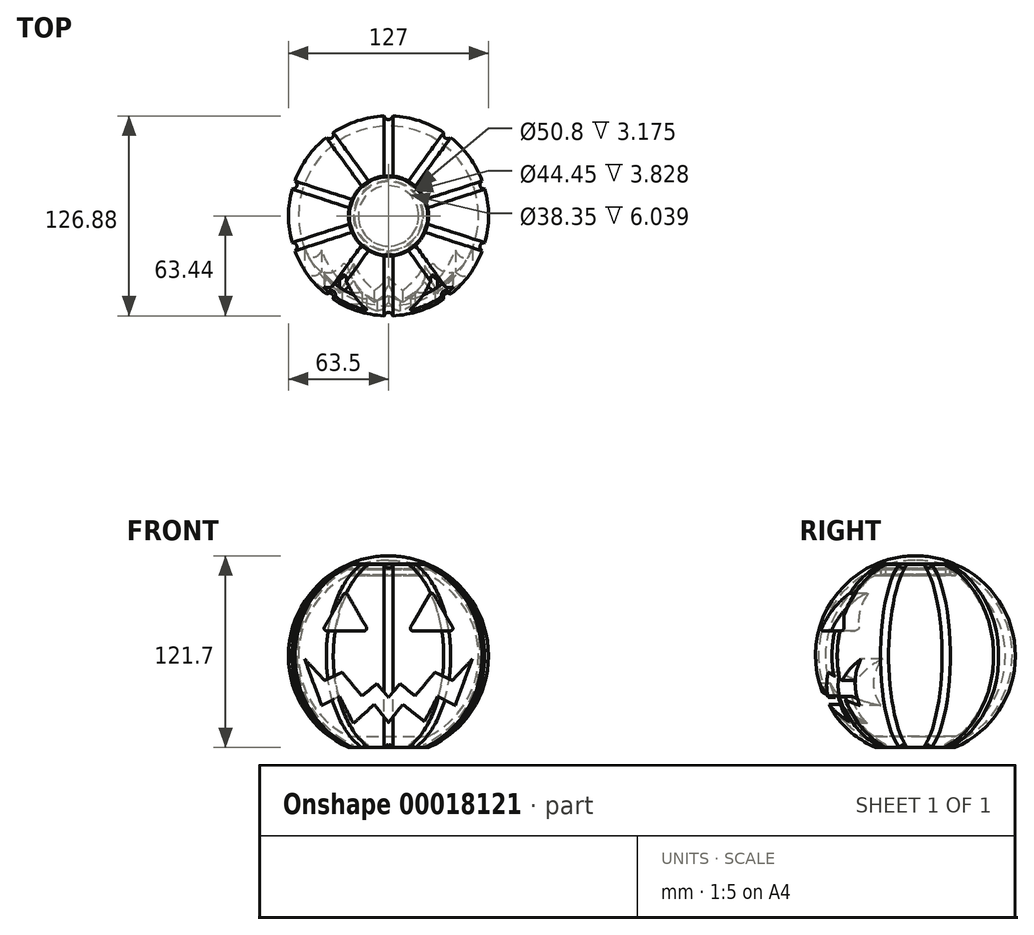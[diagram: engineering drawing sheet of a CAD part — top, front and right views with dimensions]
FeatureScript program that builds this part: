
annotation { "Feature Type Name" : "Feature", "Feature Type Description" : "" }
export const myFeature = defineFeature(function(context is Context, id is Id, definition is map)
    precondition{}
    {
        {
            var Q0;
            Q0=qCreatedBy(makeId("Front.planeOp"),FACE);
            var sketch = newSketch(context, id + "F0", { "sketchPlane" : qUnion([Q0])});
            skLineSegment(sketch, "E0", {"start": v(0, 0) * mm, "end": v(0, 76.9) * mm, "construction": true});
            skSolve(sketch);
        }
        {
            var Q0;
            Q0=qCreatedBy(makeId("Front.planeOp"),FACE);
            var sketch = newSketch(context, id + "F1", { "sketchPlane" : qUnion([Q0])});
            skArc(sketch, "E1", {"start": v(25.4, -58.2) * mm, "mid": v(63.5, 0) * mm, "end": v(25.4, 58.2) * mm});
            skLineSegment(sketch, "E2", {"start": v(0, -58.2) * mm, "end": v(25.4, -58.2) * mm});
            skPoint(sketch, "E3.visualSharp", {"position": v(25.4, -58.2) * mm});
            skLineSegment(sketch, "E4", {"start": v(0, -58.2) * mm, "end": v(0, -51.2) * mm});
            skLineSegment(sketch, "E5", {"start": v(0, -51.2) * mm, "end": v(25.4, -51.2) * mm});
            skArc(sketch, "E6", {"start": v(25.4, -51.2) * mm, "mid": v(57.15, 0) * mm, "end": v(25.4, 51.2) * mm});
            skLineSegment(sketch, "E7", {"start": v(25.4, 55.02) * mm, "end": v(25.4, 58.2) * mm});
            skLineSegment(sketch, "E8", {"start": v(25.4, 51.2) * mm, "end": v(22.22, 51.2) * mm});
            skLineSegment(sketch, "E9", {"start": v(22.22, 51.2) * mm, "end": v(22.22, 55.02) * mm});
            skLineSegment(sketch, "E10", {"start": v(22.22, 55.02) * mm, "end": v(25.4, 55.02) * mm});
            skSolve(sketch);
        }
        {
            var Q0;
            Q0=makeQuery(id+"F1.imprint","IMPRINT",FACE,{"disambiguationData":[TD([[makeQuery(id+"F1.imprint","IMPRINT",EDGE,{"derivedFrom":sQuery(id+"F1.wireOp",EDGE,"E1")}),1.0]])]});
            var Q1;
            Q1=sQuery(id+"F1.wireOp",EDGE,"E1");
            var Q2;
            Q2=sQuery(id+"F1.wireOp",EDGE,"E2");
            var Q3;
            Q3=sQuery(id+"F1.wireOp",EDGE,"E3.filletArc");
            var Q4;
            Q4=sQuery(id+"F0.wireOp",EDGE,"E0");
            revolve(context, id + "F2", {"entities" : qUnion([Q0]), "surfaceEntities" : qUnion([Q1, Q2, Q3]), "axis" : qUnion([Q4]), "revolveType" : RevolveType.FULL});
        }
        {
            var Q0;
            Q0=qCreatedBy(makeId("Right.planeOp"),FACE);
            var sketch = newSketch(context, id + "F3", { "sketchPlane" : qUnion([Q0])});
            skArc(sketch, "E11", {"start": v(22.23, -52.65) * mm, "mid": v(57.15, 0) * mm, "end": v(22.22, 52.65) * mm});
            skSolve(sketch);
        }
        {
            var Q0;
            Q0=sQuery(id+"F3.wireOp",EDGE,"E11");
            var Q1;
            Q1=sQuery(id+"F3.wireOp",VERTEX,"E11.start");
            cPlane(context, id + "F4", {"entities" : qUnion([Q0, Q1]), "cplaneType" : CPlaneType.CURVE_POINT, "offset" : 152.4 * mm, "width" : 152.4 * mm, "height" : 152.4 * mm});
        }
        {
            var Q0;
            Q0=qCreatedBy(id+"F4.planeOp",FACE);
            var sketch = newSketch(context, id + "F5", { "sketchPlane" : qUnion([Q0])});
            skLineSegment(sketch, "E12", {"start": v(-2.75, -63.44) * mm, "end": v(-2.2, -62.49) * mm});
            skLineSegment(sketch, "E13", {"start": v(2.2, -62.49) * mm, "end": v(2.75, -63.44) * mm});
            skPoint(sketch, "E14.visualSharp", {"position": v(0, -58.68) * mm});
            skArc(sketch, "E14.filletArc", {"start": v(2.2, -62.49) * mm, "mid": v(0, -61.22) * mm, "end": v(-2.2, -62.49) * mm});
            skArc(sketch, "E15", {"start": v(-2.75, -63.44) * mm, "mid": v(0, -63.5) * mm, "end": v(2.75, -63.44) * mm});
            skSolve(sketch);
        }
        {
            var Q0;
            Q0 = qSketchRegion(id + "F5", true);
            var Q1;
            Q1=sQuery(id+"F5.wireOp",EDGE,"E13");
            var Q2;
            Q2=sQuery(id+"F5.wireOp",EDGE,"E14.filletArc");
            var Q3;
            Q3=sQuery(id+"F5.wireOp",EDGE,"E12");
            var Q4;
            Q4=sQuery(id+"F5.wireOp",EDGE,"31aaabd7-cd06-456e-b9bc-34f2f859033a");
            var Q5;
            Q5=sQuery(id+"F3.wireOp",EDGE,"E11");
            sweep(context, id + "F6", {"profiles" : qUnion([Q0]), "surfaceProfiles" : qUnion([Q1, Q2, Q3, Q4]), "path" : qUnion([Q5])});
        }
        {
            var Q0;
            Q0=makeQuery(id+"F6.opSweep","SWEPT_BODY",BODY,{"disambiguationData":[OSD([sQuery(id+"F3.wireOp",EDGE,"E11"),sQuery(id+"F5.wireOp",EDGE,"E12"),sQuery(id+"F5.wireOp",EDGE,"E13"),sQuery(id+"F5.wireOp",EDGE,"E14.filletArc"),sQuery(id+"F5.wireOp",EDGE,"E15")])]});
            var Q1;
            Q1=sQuery(id+"F0.wireOp",EDGE,"E0");
            circularPattern(context, id + "F7", {"entities" : qUnion([Q0]), "axis" : qUnion([Q1]), "angle" : 360 * degree, "instanceCount" : 10, "equalSpace" : true});
        }
        {
            var Q0;
            Q0=makeQuery(id+"F6.opSweep","SWEPT_BODY",BODY,{"disambiguationData":[OSD([sQuery(id+"F3.wireOp",EDGE,"E11"),sQuery(id+"F5.wireOp",EDGE,"E12"),sQuery(id+"F5.wireOp",EDGE,"E13"),sQuery(id+"F5.wireOp",EDGE,"E14.filletArc"),sQuery(id+"F5.wireOp",EDGE,"E15")])]});
            var Q1;
            Q1=makeQuery(id+"F7.opPattern","COPY",BODY,{"derivedFrom":makeQuery(id+"F6.opSweep","SWEPT_BODY",BODY,{"disambiguationData":[OSD([sQuery(id+"F3.wireOp",EDGE,"E11"),sQuery(id+"F5.wireOp",EDGE,"E12"),sQuery(id+"F5.wireOp",EDGE,"E13"),sQuery(id+"F5.wireOp",EDGE,"E14.filletArc"),sQuery(id+"F5.wireOp",EDGE,"E15")])]}),"instanceName":"1"});
            var Q2;
            Q2=makeQuery(id+"F7.opPattern","COPY",BODY,{"derivedFrom":makeQuery(id+"F6.opSweep","SWEPT_BODY",BODY,{"disambiguationData":[OSD([sQuery(id+"F3.wireOp",EDGE,"E11"),sQuery(id+"F5.wireOp",EDGE,"E12"),sQuery(id+"F5.wireOp",EDGE,"E13"),sQuery(id+"F5.wireOp",EDGE,"E14.filletArc"),sQuery(id+"F5.wireOp",EDGE,"E15")])]}),"instanceName":"2"});
            var Q3;
            Q3=makeQuery(id+"F7.opPattern","COPY",BODY,{"derivedFrom":makeQuery(id+"F6.opSweep","SWEPT_BODY",BODY,{"disambiguationData":[OSD([sQuery(id+"F3.wireOp",EDGE,"E11"),sQuery(id+"F5.wireOp",EDGE,"E12"),sQuery(id+"F5.wireOp",EDGE,"E13"),sQuery(id+"F5.wireOp",EDGE,"E14.filletArc"),sQuery(id+"F5.wireOp",EDGE,"E15")])]}),"instanceName":"3"});
            var Q4;
            Q4=makeQuery(id+"F7.opPattern","COPY",BODY,{"derivedFrom":makeQuery(id+"F6.opSweep","SWEPT_BODY",BODY,{"disambiguationData":[OSD([sQuery(id+"F3.wireOp",EDGE,"E11"),sQuery(id+"F5.wireOp",EDGE,"E12"),sQuery(id+"F5.wireOp",EDGE,"E13"),sQuery(id+"F5.wireOp",EDGE,"E14.filletArc"),sQuery(id+"F5.wireOp",EDGE,"E15")])]}),"instanceName":"4"});
            var Q5;
            Q5=makeQuery(id+"F7.opPattern","COPY",BODY,{"derivedFrom":makeQuery(id+"F6.opSweep","SWEPT_BODY",BODY,{"disambiguationData":[OSD([sQuery(id+"F3.wireOp",EDGE,"E11"),sQuery(id+"F5.wireOp",EDGE,"E12"),sQuery(id+"F5.wireOp",EDGE,"E13"),sQuery(id+"F5.wireOp",EDGE,"E14.filletArc"),sQuery(id+"F5.wireOp",EDGE,"E15")])]}),"instanceName":"5"});
            var Q6;
            Q6=makeQuery(id+"F7.opPattern","COPY",BODY,{"derivedFrom":makeQuery(id+"F6.opSweep","SWEPT_BODY",BODY,{"disambiguationData":[OSD([sQuery(id+"F3.wireOp",EDGE,"E11"),sQuery(id+"F5.wireOp",EDGE,"E12"),sQuery(id+"F5.wireOp",EDGE,"E13"),sQuery(id+"F5.wireOp",EDGE,"E14.filletArc"),sQuery(id+"F5.wireOp",EDGE,"E15")])]}),"instanceName":"6"});
            var Q7;
            Q7=makeQuery(id+"F7.opPattern","COPY",BODY,{"derivedFrom":makeQuery(id+"F6.opSweep","SWEPT_BODY",BODY,{"disambiguationData":[OSD([sQuery(id+"F3.wireOp",EDGE,"E11"),sQuery(id+"F5.wireOp",EDGE,"E12"),sQuery(id+"F5.wireOp",EDGE,"E13"),sQuery(id+"F5.wireOp",EDGE,"E14.filletArc"),sQuery(id+"F5.wireOp",EDGE,"E15")])]}),"instanceName":"7"});
            var Q8;
            Q8=makeQuery(id+"F7.opPattern","COPY",BODY,{"derivedFrom":makeQuery(id+"F6.opSweep","SWEPT_BODY",BODY,{"disambiguationData":[OSD([sQuery(id+"F3.wireOp",EDGE,"E11"),sQuery(id+"F5.wireOp",EDGE,"E12"),sQuery(id+"F5.wireOp",EDGE,"E13"),sQuery(id+"F5.wireOp",EDGE,"E14.filletArc"),sQuery(id+"F5.wireOp",EDGE,"E15")])]}),"instanceName":"8"});
            var Q9;
            Q9=makeQuery(id+"F7.opPattern","COPY",BODY,{"derivedFrom":makeQuery(id+"F6.opSweep","SWEPT_BODY",BODY,{"disambiguationData":[OSD([sQuery(id+"F3.wireOp",EDGE,"E11"),sQuery(id+"F5.wireOp",EDGE,"E12"),sQuery(id+"F5.wireOp",EDGE,"E13"),sQuery(id+"F5.wireOp",EDGE,"E14.filletArc"),sQuery(id+"F5.wireOp",EDGE,"E15")])]}),"instanceName":"9"});
            var Q10;
            Q10=makeQuery(id+"F2.opRevolve","SWEPT_BODY",BODY,{"disambiguationData":[OSD([sQuery(id+"F1.wireOp",EDGE,"E1"),sQuery(id+"F1.wireOp",EDGE,"E2"),sQuery(id+"F1.wireOp",EDGE,"E4"),sQuery(id+"F1.wireOp",EDGE,"E5"),sQuery(id+"F1.wireOp",EDGE,"E6"),sQuery(id+"F1.wireOp",EDGE,"E7")])]});
            booleanBodies(context, id + "F8", {"operationType" : BooleanOperationType.SUBTRACTION, "tools" : qUnion([Q0, Q1, Q2, Q3, Q4, Q5, Q6, Q7, Q8, Q9]), "targets" : qUnion([Q10])});
        }
        {
            var Q0;
            Q0=qCreatedBy(makeId("Right.planeOp"),FACE);
            var sketch = newSketch(context, id + "F9", { "sketchPlane" : qUnion([Q0])});
            skPoint(sketch, "E16", {"position": v(-63.44, 0) * mm});
            skSolve(sketch);
        }
        {
            var Q0;
            Q0=qCreatedBy(makeId("Front.planeOp"),FACE);
            var Q1;
            Q1=sQuery(id+"F9.wireOp",VERTEX,"E16");
            cPlane(context, id + "F10", {"entities" : qUnion([Q0, Q1]), "cplaneType" : CPlaneType.PLANE_POINT, "offset" : 152.4 * mm, "width" : 152.4 * mm, "height" : 152.4 * mm});
        }
        {
            var Q0;
            Q0=qCreatedBy(id+"F10.planeOp",FACE);
            var sketch = newSketch(context, id + "F11", { "sketchPlane" : qUnion([Q0])});
            skLineSegment(sketch, "E17", {"start": v(-39.28, 15.88) * mm, "end": v(-15.45, 15.88) * mm});
            skLineSegment(sketch, "E18", {"start": v(-14.07, 18.26) * mm, "end": v(-25.99, 38.9) * mm});
            skLineSegment(sketch, "E19", {"start": v(-28.74, 38.9) * mm, "end": v(-40.65, 18.26) * mm});
            skLineSegment(sketch, "E20", {"start": v(15.45, 15.88) * mm, "end": v(39.28, 15.87) * mm});
            skLineSegment(sketch, "E21", {"start": v(40.65, 18.26) * mm, "end": v(28.74, 38.9) * mm});
            skLineSegment(sketch, "E22", {"start": v(25.99, 38.9) * mm, "end": v(14.07, 18.26) * mm});
            skLineSegment(sketch, "E23", {"start": v(0, 0) * mm, "end": v(0, 94.66) * mm, "construction": true});
            skPoint(sketch, "E24.visualSharp", {"position": v(-12.7, 15.88) * mm});
            skArc(sketch, "E24.filletArc", {"start": v(-15.45, 15.87) * mm, "mid": v(-14.07, 16.67) * mm, "end": v(-14.07, 18.26) * mm});
            skPoint(sketch, "E25.visualSharp", {"position": v(-42.03, 15.88) * mm});
            skArc(sketch, "E25.filletArc", {"start": v(-40.65, 18.26) * mm, "mid": v(-40.65, 16.67) * mm, "end": v(-39.28, 15.87) * mm});
            skPoint(sketch, "E26.visualSharp", {"position": v(-27.36, 41.27) * mm});
            skArc(sketch, "E26.filletArc", {"start": v(-25.99, 38.9) * mm, "mid": v(-27.36, 39.69) * mm, "end": v(-28.74, 38.9) * mm});
            skPoint(sketch, "E27.visualSharp", {"position": v(27.36, 41.27) * mm});
            skArc(sketch, "E27.filletArc", {"start": v(28.74, 38.9) * mm, "mid": v(27.36, 39.69) * mm, "end": v(25.99, 38.9) * mm});
            skPoint(sketch, "E28.visualSharp", {"position": v(42.03, 15.88) * mm});
            skArc(sketch, "E28.filletArc", {"start": v(39.28, 15.87) * mm, "mid": v(40.65, 16.67) * mm, "end": v(40.65, 18.26) * mm});
            skPoint(sketch, "E29.visualSharp", {"position": v(12.7, 15.88) * mm});
            skArc(sketch, "E29.filletArc", {"start": v(14.07, 18.26) * mm, "mid": v(14.07, 16.67) * mm, "end": v(15.45, 15.87) * mm});
            skSolve(sketch);
        }
        {
            var Q0;
            Q0=makeQuery(id+"F11.imprint","IMPRINT",FACE,{"disambiguationData":[TD([[makeQuery(id+"F11.imprint","IMPRINT",EDGE,{"derivedFrom":sQuery(id+"F11.wireOp",EDGE,"E17")}),1.0]])]});
            var Q1;
            Q1=makeQuery(id+"F11.imprint","IMPRINT",FACE,{"disambiguationData":[TD([[makeQuery(id+"F11.imprint","IMPRINT",EDGE,{"derivedFrom":sQuery(id+"F11.wireOp",EDGE,"E20")}),1.0]])]});
            var Q2;
            Q2=makeQuery(id+"F2.opRevolve","SWEPT_FACE",FACE,{"disambiguationData":[OSD([sQuery(id+"F1.wireOp",EDGE,"E6")])]});
            extrude(context, id + "F12", {"entities" : qUnion([Q0, Q1]), "operationType" : NewBodyOperationType.REMOVE, "endBound" : BoundingType.UP_TO_SURFACE, "oppositeDirection" : true, "endBoundEntityFace" : qUnion([Q2]), "depth" : 25.4 * mm});
        }
        {
            var Q0;
            Q0=qCreatedBy(id+"F10.planeOp",FACE);
            var sketch = newSketch(context, id + "F13", { "sketchPlane" : qUnion([Q0])});
            skLineSegment(sketch, "E30", {"start": v(0, 0) * mm, "end": v(0, 83.02) * mm, "construction": true});
            skLineSegment(sketch, "E31", {"start": v(-29.47, -10.47) * mm, "end": v(-16.84, -25.55) * mm});
            skLineSegment(sketch, "E32", {"start": v(-16.84, -25.55) * mm, "end": v(-7.4, -17.63) * mm});
            skLineSegment(sketch, "E33", {"start": v(-7.4, -17.63) * mm, "end": v(0, -26.45) * mm});
            skLineSegment(sketch, "E34", {"start": v(0, -26.45) * mm, "end": v(7.4, -17.63) * mm});
            skLineSegment(sketch, "E35", {"start": v(7.4, -17.63) * mm, "end": v(16.84, -25.55) * mm});
            skLineSegment(sketch, "E36", {"start": v(16.84, -25.55) * mm, "end": v(29.47, -10.47) * mm});
            skLineSegment(sketch, "E37", {"start": v(29.47, -10.47) * mm, "end": v(40.54, -15.6) * mm});
            skLineSegment(sketch, "E38", {"start": v(40.54, -15.6) * mm, "end": v(53.23, -2.1) * mm});
            skLineSegment(sketch, "E39", {"start": v(53.23, -2.1) * mm, "end": v(42.43, -31.53) * mm});
            skLineSegment(sketch, "E40", {"start": v(42.43, -31.53) * mm, "end": v(31.18, -25.73) * mm});
            skLineSegment(sketch, "E41", {"start": v(31.18, -25.73) * mm, "end": v(22.9, -41.77) * mm});
            skLineSegment(sketch, "E42", {"start": v(22.9, -41.77) * mm, "end": v(9.04, -30.85) * mm});
            skLineSegment(sketch, "E43", {"start": v(9.04, -30.85) * mm, "end": v(0, -42.32) * mm});
            skLineSegment(sketch, "E44", {"start": v(0, -42.32) * mm, "end": v(-9.04, -30.85) * mm});
            skLineSegment(sketch, "E45", {"start": v(-9.04, -30.85) * mm, "end": v(-22.27, -43) * mm});
            skLineSegment(sketch, "E46", {"start": v(-29.47, -10.47) * mm, "end": v(-40.54, -15.6) * mm});
            skLineSegment(sketch, "E47", {"start": v(-40.54, -15.6) * mm, "end": v(-53.23, -2.1) * mm});
            skLineSegment(sketch, "E48", {"start": v(-53.23, -2.1) * mm, "end": v(-42.43, -31.53) * mm});
            skLineSegment(sketch, "E49", {"start": v(-42.43, -31.53) * mm, "end": v(-31.18, -25.73) * mm});
            skLineSegment(sketch, "E50", {"start": v(-31.18, -25.73) * mm, "end": v(-22.27, -43) * mm});
            skSolve(sketch);
        }
        {
            var Q0;
            Q0=makeQuery(id+"F13.imprint","IMPRINT",FACE,{"disambiguationData":[TD([[makeQuery(id+"F13.imprint","IMPRINT",EDGE,{"derivedFrom":sQuery(id+"F13.wireOp",EDGE,"E31")}),-1.0]])]});
            var Q1;
            Q1=sQuery(id+"F13.wireOp",EDGE,"E32");
            var Q2;
            Q2=makeQuery(id+"F2.opRevolve","SWEPT_FACE",FACE,{"disambiguationData":[OSD([sQuery(id+"F1.wireOp",EDGE,"E6")])]});
            extrude(context, id + "F14", {"entities" : qUnion([Q0]), "operationType" : NewBodyOperationType.REMOVE, "surfaceEntities" : qUnion([Q1]), "endBound" : BoundingType.UP_TO_SURFACE, "oppositeDirection" : true, "endBoundEntityFace" : qUnion([Q2]), "depth" : 25.4 * mm});
        }
        {
            var Q0;
            Q0=qCreatedBy(makeId("Front.planeOp"),FACE);
            var sketch = newSketch(context, id + "F15", { "sketchPlane" : qUnion([Q0])});
            skLineSegment(sketch, "E51", {"start": v(0, 52.55) * mm, "end": v(0, 77.6) * mm, "construction": true});
            skLineSegment(sketch, "E52", {"start": v(-21.72, 51.56) * mm, "end": v(-19.18, 51.56) * mm});
            skLineSegment(sketch, "E53", {"start": v(-19.18, 51.56) * mm, "end": v(-19.18, 57.6) * mm});
            skArc(sketch, "E54", {"start": v(0, 63.5) * mm, "mid": v(-12.7, 62.22) * mm, "end": v(-24.9, 58.42) * mm});
            skLineSegment(sketch, "E55", {"start": v(-24.9, 58.42) * mm, "end": v(-24.9, 55.37) * mm});
            skLineSegment(sketch, "E56", {"start": v(-24.9, 55.37) * mm, "end": v(-21.72, 55.37) * mm});
            skLineSegment(sketch, "E57", {"start": v(-21.72, 55.37) * mm, "end": v(-21.72, 51.56) * mm});
            skArc(sketch, "E58", {"start": v(0, 60.7) * mm, "mid": v(-9.71, 59.92) * mm, "end": v(-19.18, 57.6) * mm});
            skLineSegment(sketch, "E59", {"start": v(0, 60.7) * mm, "end": v(0, 63.5) * mm});
            skSolve(sketch);
        }
        {
            var Q0;
            Q0=makeQuery(id+"F15.imprint","IMPRINT",FACE,{"disambiguationData":[TD([[makeQuery(id+"F15.imprint","IMPRINT",EDGE,{"derivedFrom":sQuery(id+"F15.wireOp",EDGE,"E52")}),1.0]])]});
            var Q1;
            Q1=sQuery(id+"F15.wireOp",EDGE,"E51");
            revolve(context, id + "F16", {"entities" : qUnion([Q0]), "axis" : qUnion([Q1]), "revolveType" : RevolveType.FULL});
        }
    });
